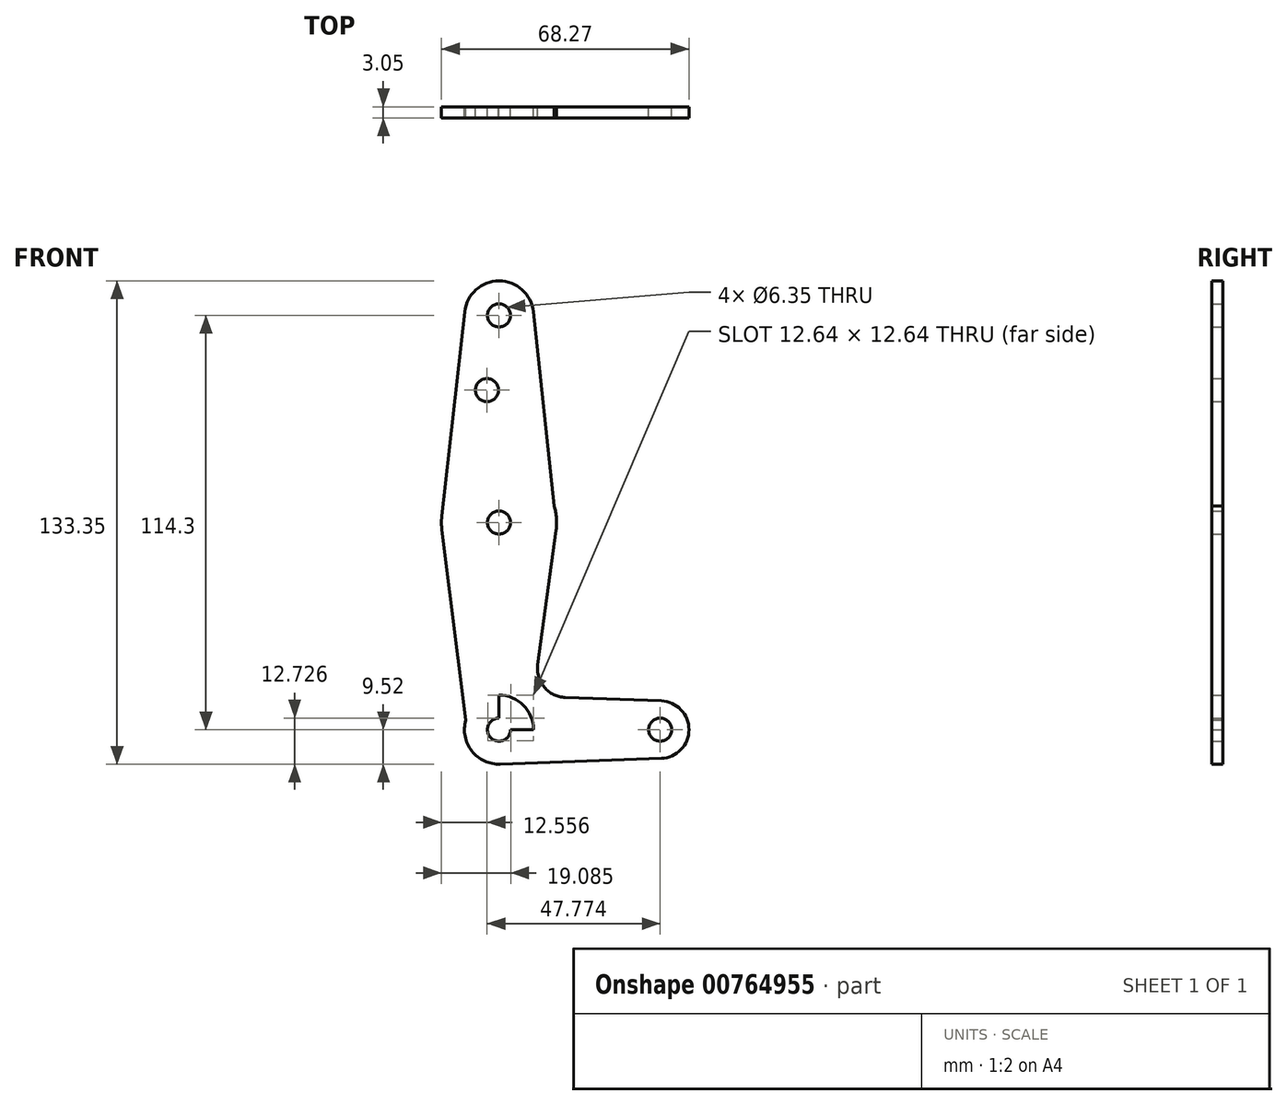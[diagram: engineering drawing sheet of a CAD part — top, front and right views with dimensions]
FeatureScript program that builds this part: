
annotation { "Feature Type Name" : "Feature", "Feature Type Description" : "" }
export const myFeature = defineFeature(function(context is Context, id is Id, definition is map)
    precondition{}
    {
        {
            var Q0;
            Q0=qCreatedBy(makeId("Front.planeOp"),FACE);
            var sketch = newSketch(context, id + "F0", { "sketchPlane" : qUnion([Q0])});
            skLineSegment(sketch, "E0", {"start": v(0, 114.3) * mm, "end": v(0, 0) * mm});
            skLineSegment(sketch, "E1", {"start": v(0, 0) * mm, "end": v(44.45, 0) * mm});
            skCircle(sketch, "E2", {"center": v(0, 114.3) * mm, "radius": 9.53 * mm});
            skCircle(sketch, "E3", {"center": v(0, 57.15) * mm, "radius": 15.88 * mm});
            skCircle(sketch, "E4", {"center": v(0, 0) * mm, "radius": 9.53 * mm});
            skCircle(sketch, "E5", {"center": v(44.45, 0) * mm, "radius": 7.94 * mm});
            skLineSegment(sketch, "E6", {"start": v(-9.47, 115.36) * mm, "end": v(-15.78, 58.91) * mm});
            skLineSegment(sketch, "E7", {"start": v(9.47, 115.31) * mm, "end": v(15.22, 61.67) * mm});
            skLineSegment(sketch, "E8", {"start": v(-15.75, 55.17) * mm, "end": v(-9.16, 2.61) * mm});
            skLineSegment(sketch, "E9", {"start": v(15.73, 55.01) * mm, "end": v(10.69, 17.9) * mm});
            skLineSegment(sketch, "E10", {"start": v(18.28, 8.88) * mm, "end": v(44.73, 7.93) * mm});
            skLineSegment(sketch, "E11", {"start": v(0.34, -9.52) * mm, "end": v(44.73, -7.93) * mm});
            skCircle(sketch, "E12", {"center": v(-3.32, 93.68) * mm, "radius": 3.18 * mm});
            skCircle(sketch, "E13", {"center": v(0, 114.3) * mm, "radius": 3.18 * mm});
            skCircle(sketch, "E14", {"center": v(0, 57.15) * mm, "radius": 3.18 * mm});
            skCircle(sketch, "E15", {"center": v(0, 0) * mm, "radius": 3.18 * mm});
            skCircle(sketch, "E16", {"center": v(44.45, 0) * mm, "radius": 3.18 * mm});
            skArc(sketch, "E17.filletArc", {"start": v(10.69, 17.9) * mm, "mid": v(12.49, 11.7) * mm, "end": v(18.28, 8.88) * mm});
            skSolve(sketch);
        }
        {
            var Q0;
            Q0 = qSketchRegion(id + "F0", true);
            extrude(context, id + "F1", {"entities" : qUnion([Q0]), "depth" : 3.05 * mm, "offsetDistance" : 25.4 * mm});
        }
    });
